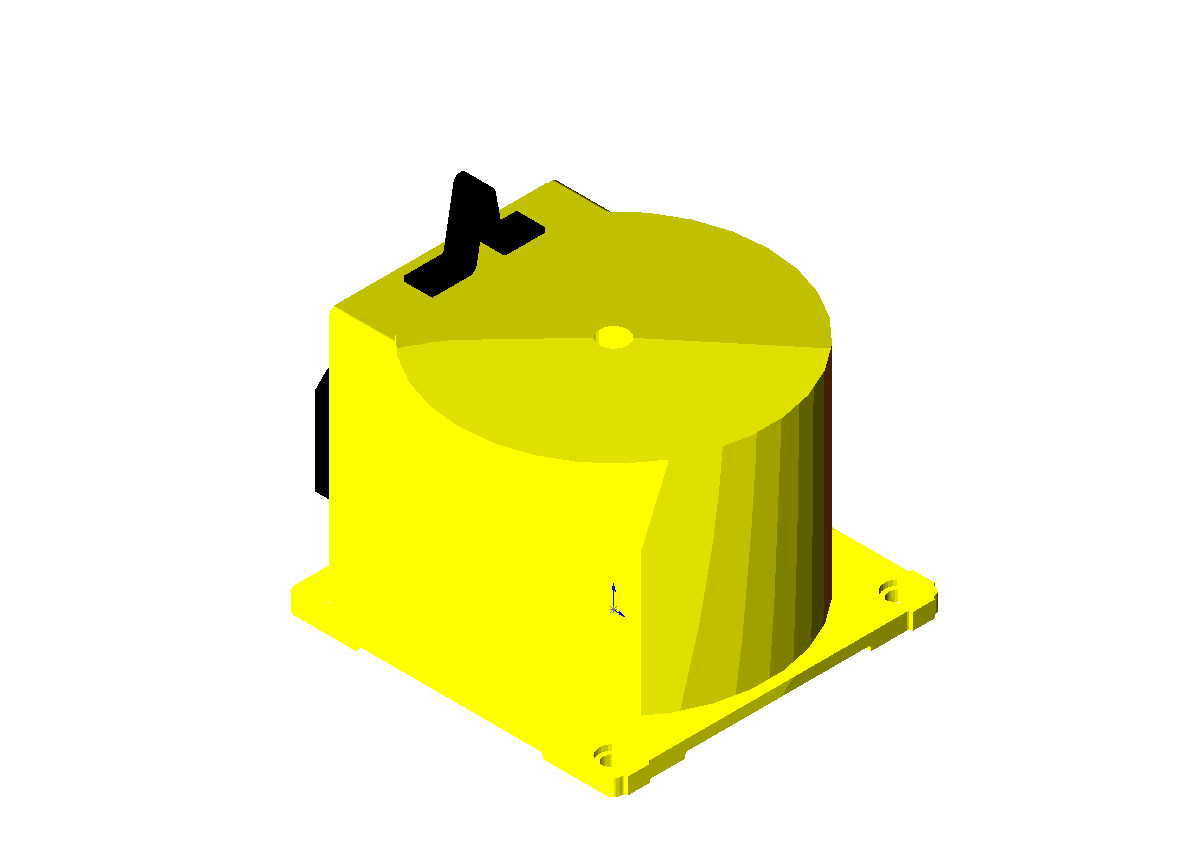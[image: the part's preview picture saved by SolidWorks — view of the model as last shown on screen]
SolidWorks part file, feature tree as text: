
SOLIDWORKS PART (.sldprt)
format: sldprt  version: not decoded by parser v0  size: 1,259,008 bytes
history: native  units: mm
features: sketch x16, extrude x7, cut_extrude x6, plane x4, material x1 (+9 scaffold rows collapsed)
feature tree (43):
  scaffold x9  (default folders/planes/origin — collapsed)
  material  "Material <not specified>"
  plane  "FRONT"
  plane  "TOP"
  plane  "SIDE"
  sketch  "Sketch1"
  sketch  "Sketch2"
  sketch  "Sketch5"
  sketch  "Sketch3"
  extrude  "Base-Extrude"  Depth=14.9225mm
  sketch  "Sketch4"
  cut_extrude  "Cut-Extrude1"  [1 undecoded]
  sketch  "Sketch6"
  cut_extrude  "Cut-Extrude2"  [1 undecoded]
  sketch  "Sketch7"
  cut_extrude  "Cut-Extrude3"  Depth=5mm
  sketch  "Sketch8"
  cut_extrude  "Cut-Extrude4"  [1 undecoded]
  sketch  "Sketch9"
  extrude  "Boss-Extrude1"  Depth=200.152mm
  sketch  "Sketch10"
  extrude  "Boss-Extrude2"  [1 undecoded]
  sketch  "Sketch11"
  extrude  "Boss-Extrude3"  Depth=14.097mm
  sketch  "Sketch12"
  extrude  "Boss-Extrude4"  Depth=2.667mm
  sketch  "Sketch13"
  extrude  "Boss-Extrude5"  Depth=34.0995mm
  sketch  "Sketch14"  dims[D1=90.0deg D2=90.0deg]
  cut_extrude  "Cut-Extrude5"  Depth=17.272mm
  plane  "Plane1"  Offset=139.78553mm
  sketch  "Sketch15"
  extrude  "Boss-Extrude6"  Depth=25.8445mm
  sketch  "Sketch16"
  cut_extrude  "Cut-Extrude6"  [1 undecoded]
decode coverage: 9 of 29 modeling features carry decoded parameters
note: 5 parameter values undecoded
summary: no parameter record found for 5 features
note: suppression state not decoded; provenance and decode notes live in map.json
